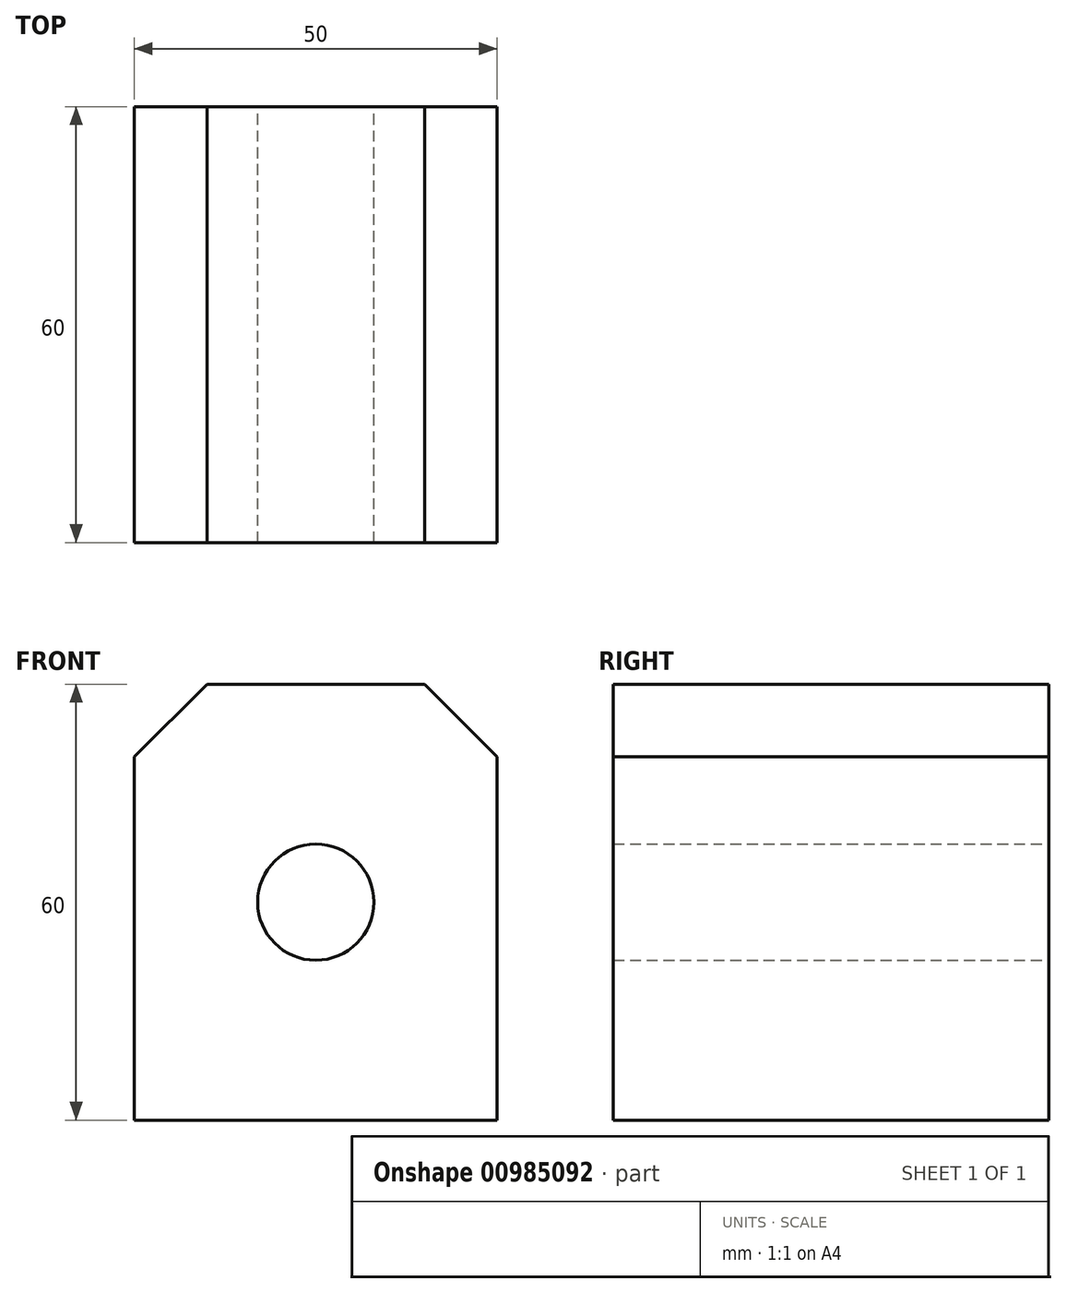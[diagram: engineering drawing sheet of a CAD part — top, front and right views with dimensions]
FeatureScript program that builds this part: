
annotation { "Feature Type Name" : "Feature", "Feature Type Description" : "" }
export const myFeature = defineFeature(function(context is Context, id is Id, definition is map)
    precondition{}
    {
        {
            var Q0;
            Q0=qCreatedBy(makeId("Front.planeOp"),FACE);
            var sketch = newSketch(context, id + "F0", { "sketchPlane" : qUnion([Q0])});
            skLineSegment(sketch, "E0.bottom", {"start": v(0, 0) * mm, "end": v(50, 0) * mm});
            skLineSegment(sketch, "E0.top", {"start": v(0, 60) * mm, "end": v(50, 60) * mm});
            skLineSegment(sketch, "E0.left", {"start": v(0, 0) * mm, "end": v(0, 60) * mm});
            skLineSegment(sketch, "E0.right", {"start": v(50, 0) * mm, "end": v(50, 60) * mm});
            skCircle(sketch, "E1", {"center": v(25, 30) * mm, "radius": 8 * mm});
            skPoint(sketch, "E2", {"position": v(0, 30) * mm});
            skPoint(sketch, "E3", {"position": v(25, 0) * mm});
            skSolve(sketch);
        }
        {
            var Q0;
            Q0=makeQuery(id+"F0.imprint","IMPRINT",FACE,{"disambiguationData":[TD([[makeQuery(id+"F0.imprint","IMPRINT",EDGE,{"derivedFrom":sQuery(id+"F0.wireOp",EDGE,"E0.bottom")}),1.0]])]});
            extrude(context, id + "F1", {"entities" : qUnion([Q0]), "depth" : 60 * mm, "offsetDistance" : 25 * mm});
        }
        {
            var Q0;
            Q0=makeQuery(id+"F1.opExtrude","SWEPT_EDGE",EDGE,{"disambiguationData":[OSD([sQuery(id+"F0.wireOp",EDGE,"E0.top"),sQuery(id+"F0.wireOp",EDGE,"E0.right")])]});
            var Q1;
            Q1=makeQuery(id+"F1.opExtrude","SWEPT_EDGE",EDGE,{"disambiguationData":[OSD([sQuery(id+"F0.wireOp",EDGE,"E0.top"),sQuery(id+"F0.wireOp",EDGE,"E0.left")])]});
            chamfer(context, id + "F2", {"entities" : qUnion([Q0, Q1]), "width" : 10 * mm, "tangentPropagation" : true});
        }
    });
